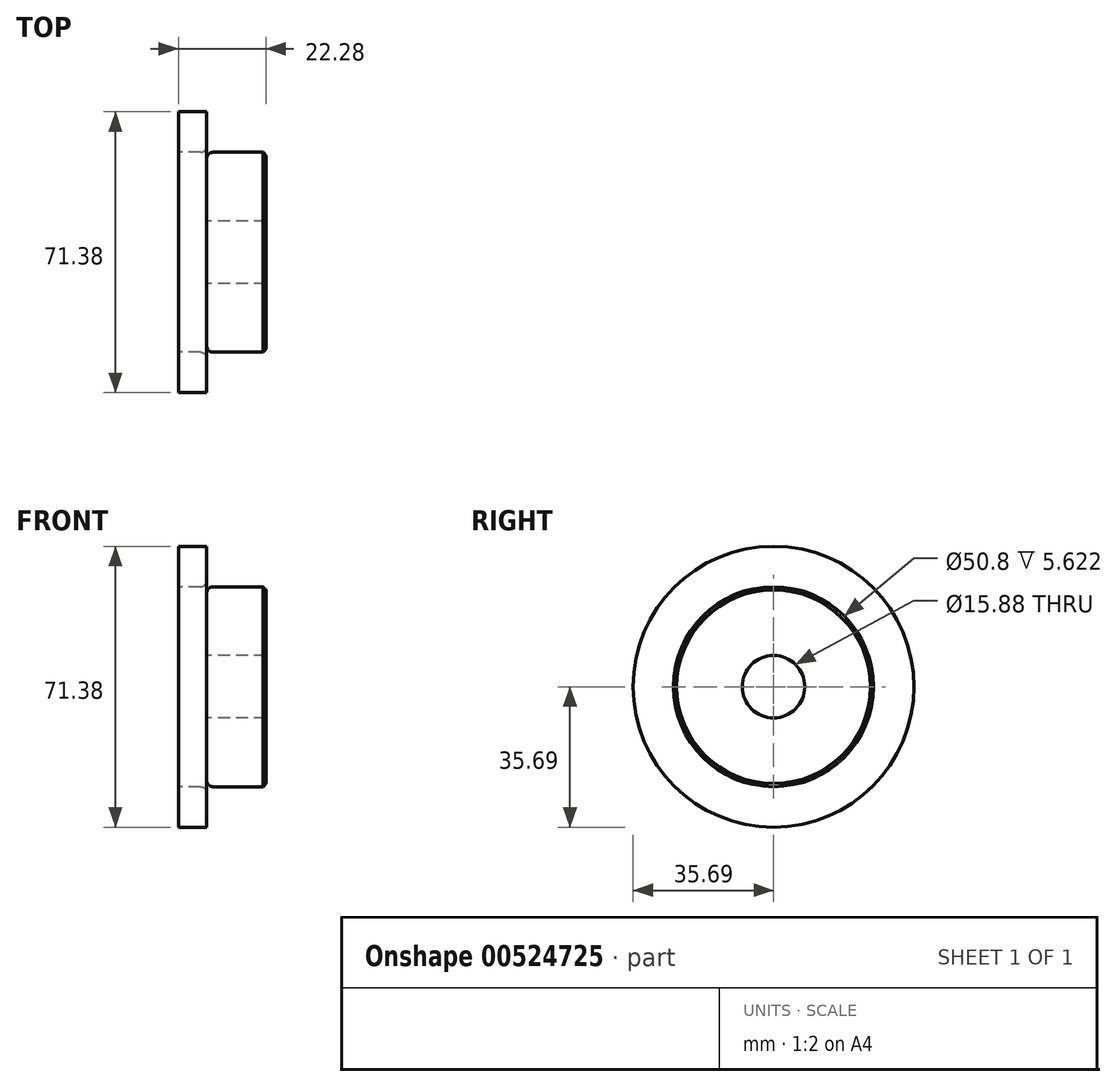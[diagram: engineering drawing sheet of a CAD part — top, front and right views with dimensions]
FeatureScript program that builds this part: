
annotation { "Feature Type Name" : "Feature", "Feature Type Description" : "" }
export const myFeature = defineFeature(function(context is Context, id is Id, definition is map)
    precondition{}
    {
        {
            var Q0;
            Q0=qCreatedBy(makeId("Front.planeOp"),FACE);
            var sketch = newSketch(context, id + "F0", { "sketchPlane" : qUnion([Q0])});
            skLineSegment(sketch, "E0", {"start": v(0, 0) * mm, "end": v(22.27, 0) * mm, "construction": true});
            skLineSegment(sketch, "E1.bottom", {"start": v(0, 7.94) * mm, "end": v(7.21, 7.94) * mm});
            skLineSegment(sketch, "E1.top", {"start": v(0, 35.68) * mm, "end": v(7.2, 35.68) * mm});
            skLineSegment(sketch, "E1.left", {"start": v(0, 7.94) * mm, "end": v(0, 35.68) * mm});
            skLineSegment(sketch, "E1.right", {"start": v(7.21, 7.94) * mm, "end": v(7.2, 35.68) * mm});
            skLineSegment(sketch, "E2.bottom", {"start": v(0, 7.94) * mm, "end": v(22.27, 7.94) * mm});
            skLineSegment(sketch, "E2.top", {"start": v(0, 25.4) * mm, "end": v(22.28, 25.4) * mm});
            skLineSegment(sketch, "E2.left", {"start": v(0, 7.94) * mm, "end": v(0, 25.4) * mm});
            skLineSegment(sketch, "E2.right", {"start": v(22.27, 7.94) * mm, "end": v(22.27, 25.4) * mm});
            skLineSegment(sketch, "E3.MirrorCS", {"start": v(0, -7.94) * mm, "end": v(22.27, -7.94) * mm});
            skLineSegment(sketch, "E4.MirrorCS", {"start": v(0, -7.94) * mm, "end": v(0, -25.4) * mm});
            skLineSegment(sketch, "E5.MirrorCS", {"start": v(0, -7.94) * mm, "end": v(0, -35.68) * mm});
            skLineSegment(sketch, "E6.MirrorCS", {"start": v(0, -35.69) * mm, "end": v(7.2, -35.69) * mm});
            skLineSegment(sketch, "E7.MirrorCS", {"start": v(0, -25.4) * mm, "end": v(22.28, -25.4) * mm});
            skLineSegment(sketch, "E8.MirrorCS", {"start": v(7.21, -7.94) * mm, "end": v(7.21, -35.68) * mm});
            skLineSegment(sketch, "E9.MirrorCS", {"start": v(22.27, -7.94) * mm, "end": v(22.28, -25.4) * mm});
            skSolve(sketch);
        }
        {
            var Q0;
            {var subQ5=sQuery(id+"F0.wireOp",EDGE,"E2.right");Q0=makeQuery(id+"F0.imprint","IMPRINT",FACE,{"disambiguationData":[TD([[makeQuery(id+"F0.imprint","IMPRINT",EDGE,{"derivedFrom":subQ5}),1.0]])]});}
            var Q1;
            {var subQ5=sQuery(id+"F0.wireOp",EDGE,"E2.left");Q1=makeQuery(id+"F0.imprint","IMPRINT",FACE,{"disambiguationData":[TD([[makeQuery(id+"F0.imprint","IMPRINT",EDGE,{"derivedFrom":subQ5}),-1.0]])]});}
            var Q2;
            {var subQ0=sQuery(id+"F0.wireOp",EDGE,"E1.top");Q2=makeQuery(id+"F0.imprint","IMPRINT",FACE,{"disambiguationData":[TD([[makeQuery(id+"F0.imprint","IMPRINT",EDGE,{"derivedFrom":subQ0}),-1.0]])]});}
            var Q3;
            Q3=sQuery(id+"F0.wireOp",EDGE,"E0");
            revolve(context, id + "F1", {"entities" : qUnion([Q0, Q1, Q2]), "axis" : qUnion([Q3]), "revolveType" : RevolveType.FULL});
        }
        {
            var Q0;
            Q0=makeQuery(id+"F1.opRevolve","SWEPT_EDGE",EDGE,{"disambiguationData":[OSD([sQuery(id+"F0.wireOp",EDGE,"E1.right"),sQuery(id+"F0.wireOp",EDGE,"E2.top")])]});
            fillet(context, id + "F2", {"entities" : qUnion([Q0]), "radius" : 1.59 * mm, "tangentPropagation" : true, "allowEdgeOverflow" : false});
        }
        {
            var Q0;
            Q0=makeQuery(id+"F1.opRevolve","SWEPT_EDGE",EDGE,{"disambiguationData":[OSD([sQuery(id+"F0.wireOp",EDGE,"E2.top"),sQuery(id+"F0.wireOp",EDGE,"E2.right")])]});
            chamfer(context, id + "F3", {"entities" : qUnion([Q0]), "width" : 0.8 * mm, "tangentPropagation" : true});
        }
    });
